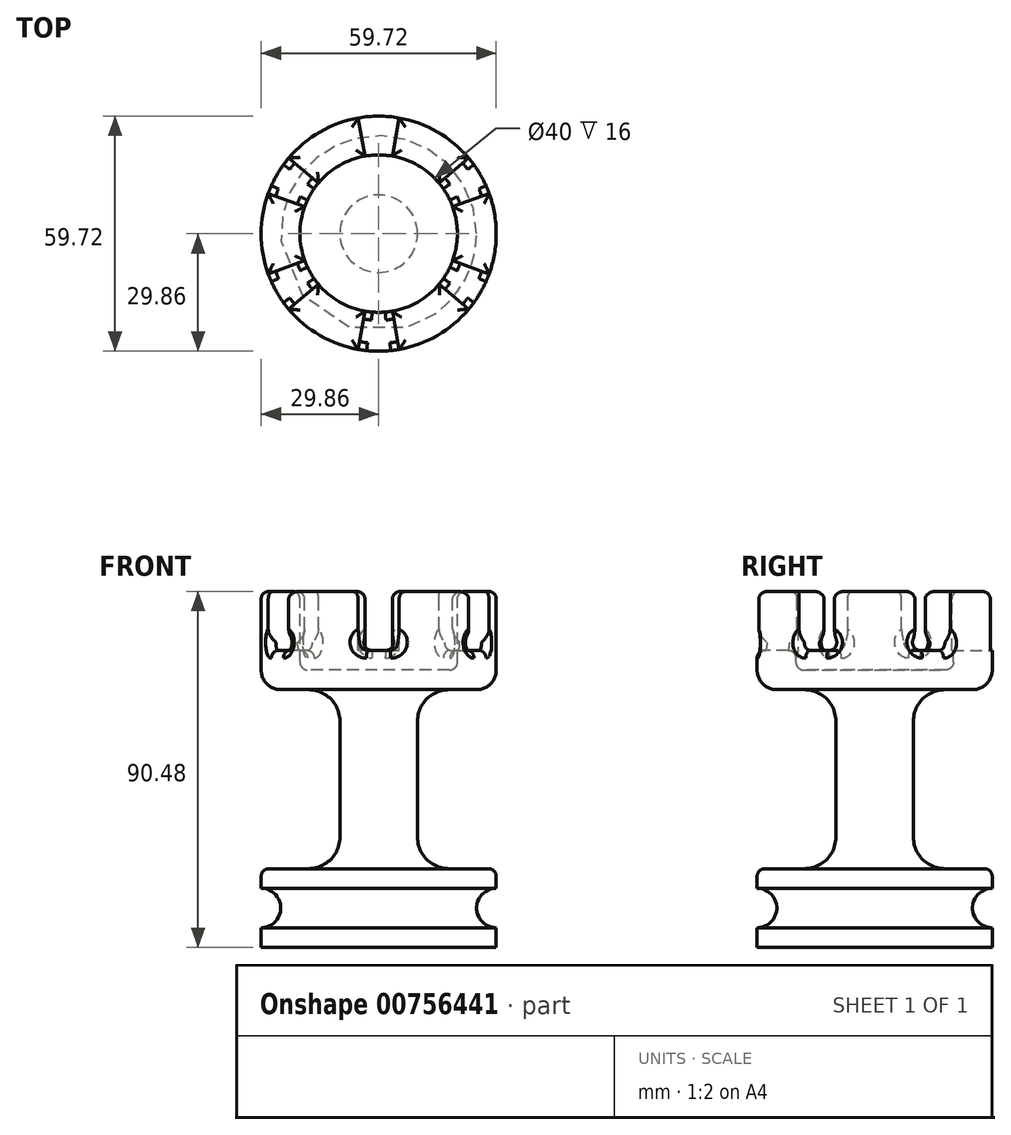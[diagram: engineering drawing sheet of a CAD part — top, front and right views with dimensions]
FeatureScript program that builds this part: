
annotation { "Feature Type Name" : "Feature", "Feature Type Description" : "" }
export const myFeature = defineFeature(function(context is Context, id is Id, definition is map)
    precondition{}
    {
        {
            var Q0;
            Q0=qCreatedBy(makeId("Front.planeOp"),FACE);
            var sketch = newSketch(context, id + "F0", { "sketchPlane" : qUnion([Q0])});
            skLineSegment(sketch, "E0.top", {"start": v(9.86, 20) * mm, "end": v(29.86, 20) * mm});
            skLineSegment(sketch, "E0.right", {"start": v(29.86, 0) * mm, "end": v(29.86, 5) * mm});
            skLineSegment(sketch, "E1.right", {"start": v(9.86, 20) * mm, "end": v(9.86, 65.48) * mm});
            skLineSegment(sketch, "E2.bottom", {"start": v(9.86, 65.48) * mm, "end": v(29.86, 65.48) * mm});
            skLineSegment(sketch, "E2.top", {"start": v(0, 90.48) * mm, "end": v(29.86, 90.48) * mm});
            skLineSegment(sketch, "E2.right", {"start": v(29.86, 65.48) * mm, "end": v(29.86, 90.48) * mm});
            skLineSegment(sketch, "E3", {"start": v(0, 90.48) * mm, "end": v(0, 0) * mm});
            skLineSegment(sketch, "E4", {"start": v(0, 0) * mm, "end": v(29.86, 0) * mm});
            skArc(sketch, "E5", {"start": v(29.86, 15) * mm, "mid": v(24.86, 10) * mm, "end": v(29.86, 5) * mm});
            skLineSegment(sketch, "E6.trimOffspring", {"start": v(29.86, 15) * mm, "end": v(29.86, 20) * mm});
            skSolve(sketch);
        }
        {
            var Q0;
            Q0=qSketchRegion(id+"F0",true);
            var Q1;
            Q1=sQuery(id+"F0.wireOp",EDGE,"E3");
            revolve(context, id + "F1", {"surfaceOperationType" : NewSurfaceOperationType.NEW, "entities" : qUnion([Q0]), "axis" : qUnion([Q1]), "revolveType" : RevolveType.FULL});
        }
        {
            var Q0;
            Q0=makeQuery(id+"F1.opRevolve","SWEPT_FACE",FACE,{"disambiguationData":[OSD([sQuery(id+"F0.wireOp",EDGE,"E2.top")])]});
            var sketch = newSketch(context, id + "F2", { "sketchPlane" : qUnion([Q0])});
            skCircle(sketch, "E7", {"center": v(0, 0) * mm, "radius": 20 * mm});
            skSolve(sketch);
        }
        {
            var Q0;
            Q0=qSketchRegion(id+"F2",true);
            extrude(context, id + "F3", {"entities" : qUnion([Q0]), "operationType" : NewBodyOperationType.REMOVE, "oppositeDirection" : true, "depth" : 20 * mm, "offsetDistance" : 25 * mm});
        }
        {
            var Q0;
            Q0=makeQuery(id+"F1.opRevolve","SWEPT_FACE",FACE,{"disambiguationData":[OSD([sQuery(id+"F0.wireOp",EDGE,"E2.top")])]});
            var sketch = newSketch(context, id + "F4", { "sketchPlane" : qUnion([Q0])});
            skLineSegment(sketch, "E8", {"start": v(3.47, 19.7) * mm, "end": v(5.2, 29.54) * mm});
            skLineSegment(sketch, "E9", {"start": v(-3.47, 19.7) * mm, "end": v(-5.2, 29.54) * mm});
            skArc(sketch, "E10", {"start": v(5.2, 29.54) * mm, "mid": v(0, 30) * mm, "end": v(-5.2, 29.54) * mm});
            skArc(sketch, "E11", {"start": v(3.47, 19.7) * mm, "mid": v(0, 20) * mm, "end": v(-3.47, 19.7) * mm});
            skLineSegment(sketch, "E12.1.0", {"start": v(-18.8, 6.84) * mm, "end": v(-28.2, 10.26) * mm});
            skArc(sketch, "E12.1.1", {"start": v(-15.32, 12.86) * mm, "mid": v(-17.32, 10) * mm, "end": v(-18.8, 6.84) * mm});
            skLineSegment(sketch, "E12.1.2", {"start": v(-15.32, 12.86) * mm, "end": v(-22.98, 19.28) * mm});
            skArc(sketch, "E12.1.3", {"start": v(-22.98, 19.28) * mm, "mid": v(-25.98, 15) * mm, "end": v(-28.2, 10.26) * mm});
            skLineSegment(sketch, "E12.2.0", {"start": v(-15.32, -12.86) * mm, "end": v(-22.98, -19.28) * mm});
            skArc(sketch, "E12.2.1", {"start": v(-18.8, -6.84) * mm, "mid": v(-17.32, -10) * mm, "end": v(-15.32, -12.86) * mm});
            skLineSegment(sketch, "E12.2.2", {"start": v(-18.8, -6.84) * mm, "end": v(-28.2, -10.26) * mm});
            skArc(sketch, "E12.2.3", {"start": v(-28.2, -10.26) * mm, "mid": v(-25.98, -15) * mm, "end": v(-22.98, -19.28) * mm});
            skLineSegment(sketch, "E12.3.0", {"start": v(3.47, -19.7) * mm, "end": v(5.2, -29.54) * mm});
            skArc(sketch, "E12.3.1", {"start": v(-3.47, -19.7) * mm, "mid": v(0, -20) * mm, "end": v(3.47, -19.7) * mm});
            skLineSegment(sketch, "E12.3.2", {"start": v(-3.47, -19.7) * mm, "end": v(-5.2, -29.54) * mm});
            skArc(sketch, "E12.3.3", {"start": v(-5.2, -29.54) * mm, "mid": v(0, -30) * mm, "end": v(5.2, -29.54) * mm});
            skLineSegment(sketch, "E12.4.0", {"start": v(18.8, -6.84) * mm, "end": v(28.2, -10.26) * mm});
            skArc(sketch, "E12.4.1", {"start": v(15.32, -12.86) * mm, "mid": v(17.32, -10) * mm, "end": v(18.8, -6.84) * mm});
            skLineSegment(sketch, "E12.4.2", {"start": v(15.32, -12.86) * mm, "end": v(22.98, -19.28) * mm});
            skArc(sketch, "E12.4.3", {"start": v(22.98, -19.28) * mm, "mid": v(25.98, -15) * mm, "end": v(28.2, -10.26) * mm});
            skLineSegment(sketch, "E12.5.0", {"start": v(15.32, 12.86) * mm, "end": v(22.98, 19.28) * mm});
            skArc(sketch, "E12.5.1", {"start": v(18.8, 6.84) * mm, "mid": v(17.32, 10) * mm, "end": v(15.32, 12.86) * mm});
            skLineSegment(sketch, "E12.5.2", {"start": v(18.8, 6.84) * mm, "end": v(28.2, 10.26) * mm});
            skArc(sketch, "E12.5.3", {"start": v(28.2, 10.26) * mm, "mid": v(25.98, 15) * mm, "end": v(22.98, 19.28) * mm});
            skSolve(sketch);
        }
        {
            var Q0;
            Q0=qSketchRegion(id+"F4",true);
            extrude(context, id + "F5", {"entities" : qUnion([Q0]), "operationType" : NewBodyOperationType.REMOVE, "oppositeDirection" : true, "depth" : 15 * mm, "offsetDistance" : 25 * mm});
        }
        {
            var Q0;
            Q0=makeQuery(id+"F1.opRevolve","SWEPT_FACE",FACE,{"disambiguationData":[OSD([sQuery(id+"F0.wireOp",EDGE,"E1.right")])]});
            fillet(context, id + "F6", {"entities" : qUnion([Q0]), "radius" : 8 * mm, "tangentPropagation" : true, "allowEdgeOverflow" : false});
        }
        {
            var Q0;
            Q0=makeQuery(id+"F1.opRevolve","SWEPT_EDGE",EDGE,{"disambiguationData":[OSD([sQuery(id+"F0.wireOp",EDGE,"E2.bottom"),sQuery(id+"F0.wireOp",EDGE,"E2.right")])]});
            fillet(context, id + "F7", {"entities" : qUnion([Q0]), "radius" : 5 * mm, "tangentPropagation" : true, "allowEdgeOverflow" : false});
        }
        {
            var Q0;
            Q0=makeQuery(id+"F1.opRevolve","SWEPT_EDGE",EDGE,{"disambiguationData":[OSD([sQuery(id+"F0.wireOp",EDGE,"E0.top"),sQuery(id+"F0.wireOp",EDGE,"E6.trimOffspring")])]});
            var Q1;
            Q1=makeQuery(id+"F5.boolean.opBoolean","SPLIT",FACE,{"disambiguationData":[TD([makeQuery(id+"F5.opExtrude","SWEPT_FACE",FACE,{"disambiguationData":[OSD([sQuery(id+"F4.wireOp",EDGE,"E12.3.0")])]})])],"derivedFrom":makeQuery(id+"F1.opRevolve","SWEPT_FACE",FACE,{"disambiguationData":[OSD([sQuery(id+"F0.wireOp",EDGE,"E2.top")])]})});
            var Q2;
            Q2=makeQuery(id+"F5.boolean.opBoolean","SPLIT",FACE,{"disambiguationData":[TD([makeQuery(id+"F5.opExtrude","SWEPT_FACE",FACE,{"disambiguationData":[OSD([sQuery(id+"F4.wireOp",EDGE,"E12.4.0")])]})])],"derivedFrom":makeQuery(id+"F1.opRevolve","SWEPT_FACE",FACE,{"disambiguationData":[OSD([sQuery(id+"F0.wireOp",EDGE,"E2.top")])]})});
            var Q3;
            Q3=makeQuery(id+"F5.boolean.opBoolean","SPLIT",FACE,{"disambiguationData":[TD([makeQuery(id+"F5.opExtrude","SWEPT_FACE",FACE,{"disambiguationData":[OSD([sQuery(id+"F4.wireOp",EDGE,"E8")])]})])],"derivedFrom":makeQuery(id+"F1.opRevolve","SWEPT_FACE",FACE,{"disambiguationData":[OSD([sQuery(id+"F0.wireOp",EDGE,"E2.top")])]})});
            var Q4;
            Q4=makeQuery(id+"F5.boolean.opBoolean","SPLIT",FACE,{"disambiguationData":[TD([makeQuery(id+"F5.opExtrude","SWEPT_FACE",FACE,{"disambiguationData":[OSD([sQuery(id+"F4.wireOp",EDGE,"E9")])]})])],"derivedFrom":makeQuery(id+"F1.opRevolve","SWEPT_FACE",FACE,{"disambiguationData":[OSD([sQuery(id+"F0.wireOp",EDGE,"E2.top")])]})});
            var Q5;
            Q5=makeQuery(id+"F5.boolean.opBoolean","SPLIT",FACE,{"disambiguationData":[TD([makeQuery(id+"F5.opExtrude","SWEPT_FACE",FACE,{"disambiguationData":[OSD([sQuery(id+"F4.wireOp",EDGE,"E12.1.0")])]})])],"derivedFrom":makeQuery(id+"F1.opRevolve","SWEPT_FACE",FACE,{"disambiguationData":[OSD([sQuery(id+"F0.wireOp",EDGE,"E2.top")])]})});
            var Q6;
            Q6=makeQuery(id+"F5.boolean.opBoolean","SPLIT",FACE,{"disambiguationData":[TD([makeQuery(id+"F5.opExtrude","SWEPT_FACE",FACE,{"disambiguationData":[OSD([sQuery(id+"F4.wireOp",EDGE,"E12.2.0")])]})])],"derivedFrom":makeQuery(id+"F1.opRevolve","SWEPT_FACE",FACE,{"disambiguationData":[OSD([sQuery(id+"F0.wireOp",EDGE,"E2.top")])]})});
            var Q7;
            Q7=makeQuery(id+"F3.boolean.opBoolean","COPY",EDGE,{"derivedFrom":makeQuery(id+"F3.opExtrude","CAP_EDGE",EDGE,{"disambiguationData":[OSD([sQuery(id+"F2.wireOp",EDGE,"E7")])],"isStart":false})});
            var Q8;
            Q8=makeQuery(id+"F5.boolean.opBoolean","COPY",FACE,{"derivedFrom":makeQuery(id+"F5.opExtrude","CAP_FACE",FACE,{"disambiguationData":[OSD([sQuery(id+"F4.wireOp",EDGE,"E12.1.0"),sQuery(id+"F4.wireOp",EDGE,"E12.1.1"),sQuery(id+"F4.wireOp",EDGE,"E12.1.2"),sQuery(id+"F4.wireOp",EDGE,"E12.1.3")])],"isStart":false})});
            var Q9;
            Q9=makeQuery(id+"F5.boolean.opBoolean","COPY",EDGE,{"derivedFrom":makeQuery(id+"F5.opExtrude","CAP_EDGE",EDGE,{"disambiguationData":[OSD([sQuery(id+"F4.wireOp",EDGE,"E11")])],"isStart":false})});
            var Q10;
            Q10=makeQuery(id+"F5.boolean.opBoolean","INTERSECT",EDGE,{"derivedFrom":[makeQuery(id+"F1.opRevolve","SWEPT_FACE",FACE,{"disambiguationData":[OSD([sQuery(id+"F0.wireOp",EDGE,"E2.right")])]}),makeQuery(id+"F5.opExtrude","CAP_FACE",FACE,{"disambiguationData":[OSD([sQuery(id+"F4.wireOp",EDGE,"E12.5.0"),sQuery(id+"F4.wireOp",EDGE,"E12.5.1"),sQuery(id+"F4.wireOp",EDGE,"E12.5.2"),sQuery(id+"F4.wireOp",EDGE,"E12.5.3")])],"isStart":false})]});
            var Q11;
            Q11=makeQuery(id+"F5.boolean.opBoolean","COPY",FACE,{"derivedFrom":makeQuery(id+"F5.opExtrude","CAP_FACE",FACE,{"disambiguationData":[OSD([sQuery(id+"F4.wireOp",EDGE,"E12.4.0"),sQuery(id+"F4.wireOp",EDGE,"E12.4.1"),sQuery(id+"F4.wireOp",EDGE,"E12.4.2"),sQuery(id+"F4.wireOp",EDGE,"E12.4.3")])],"isStart":false})});
            var Q12;
            Q12=makeQuery(id+"F5.boolean.opBoolean","COPY",FACE,{"derivedFrom":makeQuery(id+"F5.opExtrude","CAP_FACE",FACE,{"disambiguationData":[OSD([sQuery(id+"F4.wireOp",EDGE,"E12.3.0"),sQuery(id+"F4.wireOp",EDGE,"E12.3.1"),sQuery(id+"F4.wireOp",EDGE,"E12.3.2"),sQuery(id+"F4.wireOp",EDGE,"E12.3.3")])],"isStart":false})});
            var Q13;
            Q13=makeQuery(id+"F5.boolean.opBoolean","COPY",FACE,{"derivedFrom":makeQuery(id+"F5.opExtrude","CAP_FACE",FACE,{"disambiguationData":[OSD([sQuery(id+"F4.wireOp",EDGE,"E12.2.0"),sQuery(id+"F4.wireOp",EDGE,"E12.2.1"),sQuery(id+"F4.wireOp",EDGE,"E12.2.2"),sQuery(id+"F4.wireOp",EDGE,"E12.2.3")])],"isStart":false})});
            var Q14;
            Q14=makeQuery(id+"F5.boolean.opBoolean","COPY",FACE,{"derivedFrom":makeQuery(id+"F5.opExtrude","CAP_FACE",FACE,{"disambiguationData":[OSD([sQuery(id+"F4.wireOp",EDGE,"E12.5.0"),sQuery(id+"F4.wireOp",EDGE,"E12.5.1"),sQuery(id+"F4.wireOp",EDGE,"E12.5.2"),sQuery(id+"F4.wireOp",EDGE,"E12.5.3")])],"isStart":false})});
            fillet(context, id + "F8", {"entities" : qUnion([Q0, Q1, Q2, Q3, Q4, Q5, Q6, Q7, Q8, Q9, Q10, Q11, Q12, Q13, Q14]), "radius" : 2 * mm, "tangentPropagation" : true, "allowEdgeOverflow" : false});
        }
    });
